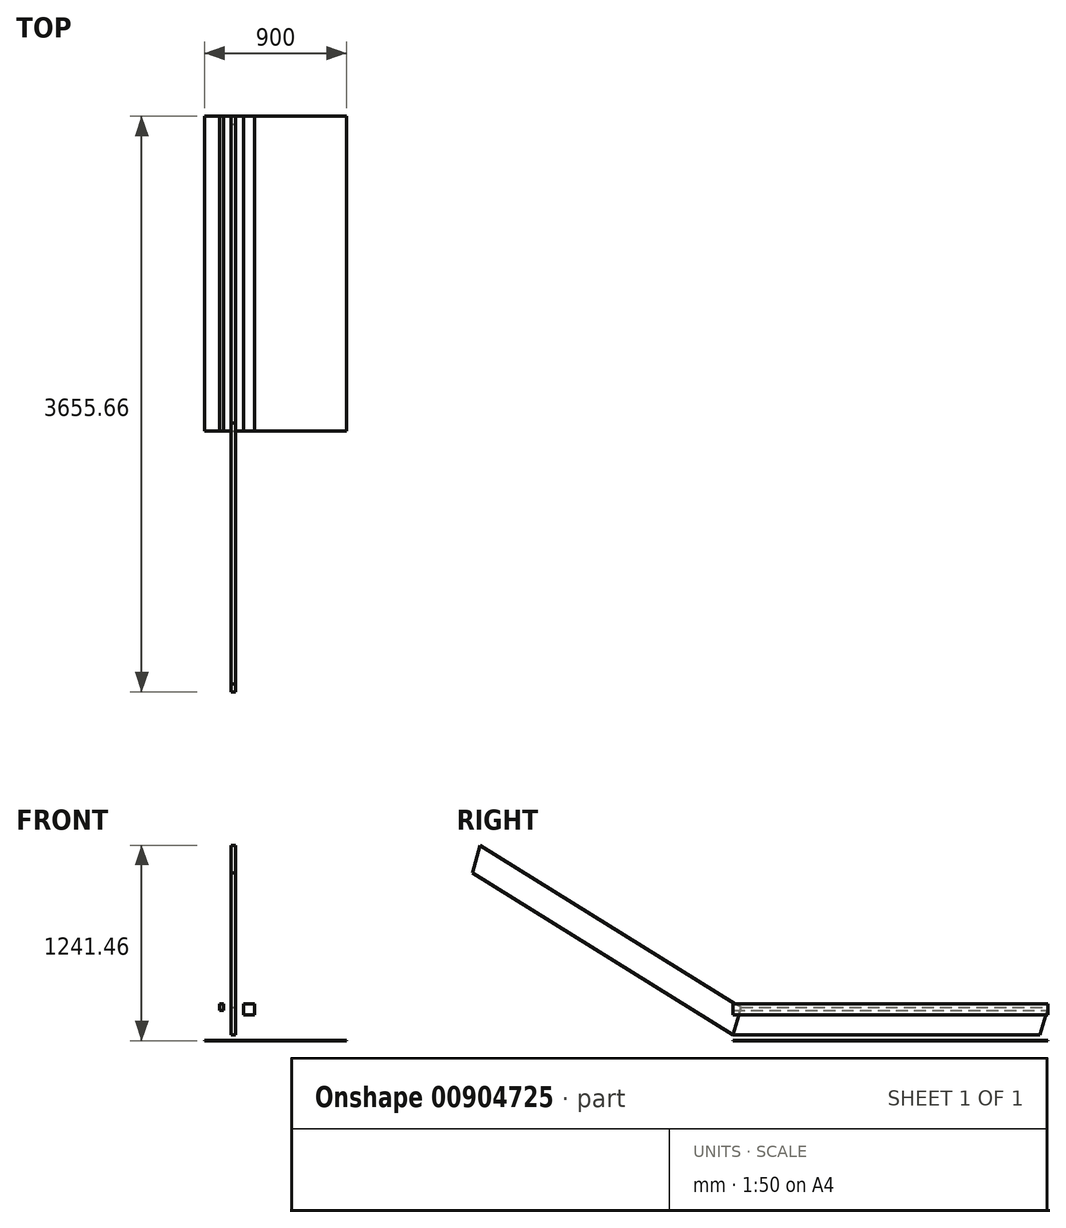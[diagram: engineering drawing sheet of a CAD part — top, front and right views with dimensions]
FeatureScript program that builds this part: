
annotation { "Feature Type Name" : "Feature", "Feature Type Description" : "" }
export const myFeature = defineFeature(function(context is Context, id is Id, definition is map)
    precondition{}
    {
        {
            var Q0;
            Q0=qCreatedBy(makeId("Front.planeOp"),FACE);
            var sketch = newSketch(context, id + "F0", { "sketchPlane" : qUnion([Q0])});
            skLineSegment(sketch, "E0.bottom", {"start": v(0, 0) * mm, "end": v(70, 0) * mm});
            skLineSegment(sketch, "E0.top", {"start": v(0, 70) * mm, "end": v(70, 70) * mm});
            skLineSegment(sketch, "E0.left", {"start": v(0, 0) * mm, "end": v(0, 70) * mm});
            skLineSegment(sketch, "E0.right", {"start": v(70, 0) * mm, "end": v(70, 70) * mm});
            skSolve(sketch);
        }
        {
            var Q0;
            Q0 = qSketchRegion(id + "F0", true);
            extrude(context, id + "F1", {"entities" : qUnion([Q0]), "depth" : 2000 * mm, "offsetDistance" : 25 * mm});
        }
        {
            var Q0;
            Q0=qCreatedBy(makeId("Front.planeOp"),FACE);
            var sketch = newSketch(context, id + "F2", { "sketchPlane" : qUnion([Q0])});
            skLineSegment(sketch, "E1.bottom", {"start": v(-81.08, 45.95) * mm, "end": v(-51.08, 45.95) * mm});
            skLineSegment(sketch, "E1.top", {"start": v(-81.08, -129.05) * mm, "end": v(-51.08, -129.05) * mm});
            skLineSegment(sketch, "E1.left", {"start": v(-81.08, 45.95) * mm, "end": v(-81.08, -129.05) * mm});
            skLineSegment(sketch, "E1.right", {"start": v(-51.08, 45.95) * mm, "end": v(-51.08, -129.05) * mm});
            skSolve(sketch);
        }
        {
            var Q0;
            Q0 = qSketchRegion(id + "F2", true);
            extrude(context, id + "F3", {"entities" : qUnion([Q0]), "depth" : 2000 * mm, "offsetDistance" : 25 * mm});
        }
        {
            var Q0;
            Q0=qCreatedBy(makeId("Front.planeOp"),FACE);
            var sketch = newSketch(context, id + "F4", { "sketchPlane" : qUnion([Q0])});
            skLineSegment(sketch, "E2.bottom", {"start": v(-153.6, 67.64) * mm, "end": v(-126.6, 67.64) * mm});
            skLineSegment(sketch, "E2.top", {"start": v(-153.6, 27.64) * mm, "end": v(-126.6, 27.64) * mm});
            skLineSegment(sketch, "E2.left", {"start": v(-153.6, 67.64) * mm, "end": v(-153.6, 27.64) * mm});
            skLineSegment(sketch, "E2.right", {"start": v(-126.6, 67.64) * mm, "end": v(-126.6, 27.64) * mm});
            skSolve(sketch);
        }
        {
            var Q0;
            Q0 = qSketchRegion(id + "F4", true);
            extrude(context, id + "F5", {"entities" : qUnion([Q0]), "depth" : 2000 * mm, "offsetDistance" : 25 * mm});
        }
        {
            var Q0;
            Q0=qCreatedBy(makeId("Front.planeOp"),FACE);
            var sketch = newSketch(context, id + "F6", { "sketchPlane" : qUnion([Q0])});
            skLineSegment(sketch, "E3.bottom", {"start": v(-247.4, -162.32) * mm, "end": v(652.6, -162.32) * mm});
            skLineSegment(sketch, "E3.top", {"start": v(-247.4, -165.32) * mm, "end": v(652.6, -165.32) * mm});
            skLineSegment(sketch, "E3.left", {"start": v(-247.4, -162.32) * mm, "end": v(-247.4, -165.32) * mm});
            skLineSegment(sketch, "E3.right", {"start": v(652.6, -162.32) * mm, "end": v(652.6, -165.32) * mm});
            skSolve(sketch);
        }
        {
            var Q0;
            Q0 = qSketchRegion(id + "F6", true);
            extrude(context, id + "F7", {"entities" : qUnion([Q0]), "depth" : 2000 * mm, "offsetDistance" : 25 * mm});
        }
        {
            var Q0;
            Q0=makeQuery(id+"F3.opExtrude","SWEPT_FACE",FACE,{"disambiguationData":[OSD([sQuery(id+"F2.wireOp",EDGE,"E1.right")])]});
            var sketch = newSketch(context, id + "F8", { "sketchPlane" : qUnion([Q0])});
            skLineSegment(sketch, "E4", {"start": v(-2000, -129.05) * mm, "end": v(-2000, 45.95) * mm});
            skLineSegment(sketch, "E5", {"start": v(-2000, 45.95) * mm, "end": v(-1950, 45.95) * mm});
            skLineSegment(sketch, "E6", {"start": v(-1950, 45.95) * mm, "end": v(-2000, -129.05) * mm});
            skLineSegment(sketch, "E7", {"start": v(0, 45.95) * mm, "end": v(0, -129.05) * mm});
            skLineSegment(sketch, "E8", {"start": v(0, -129.05) * mm, "end": v(-50, -129.05) * mm});
            skLineSegment(sketch, "E9", {"start": v(-50, -129.05) * mm, "end": v(0, 45.95) * mm});
            skSolve(sketch);
        }
        {
            var Q0;
            Q0=makeQuery(id+"F8.imprint","IMPRINT",FACE,{"disambiguationData":[TD([[makeQuery(id+"F8.imprint","IMPRINT",EDGE,{"derivedFrom":sQuery(id+"F8.wireOp",EDGE,"E7")}),-1.0]])]});
            var Q1;
            Q1=makeQuery(id+"F8.imprint","IMPRINT",FACE,{"disambiguationData":[TD([[makeQuery(id+"F8.imprint","IMPRINT",EDGE,{"derivedFrom":sQuery(id+"F8.wireOp",EDGE,"E4")}),1.0]])]});
            extrude(context, id + "F9", {"entities" : qUnion([Q0, Q1]), "operationType" : NewBodyOperationType.REMOVE, "endBound" : BoundingType.UP_TO_NEXT, "oppositeDirection" : true, "depth" : 25 * mm, "offsetDistance" : 25 * mm});
        }
        {
            var Q0;
            Q0=makeQuery(id+"F3.opExtrude","SWEPT_BODY",BODY,{"disambiguationData":[OSD([sQuery(id+"F2.wireOp",EDGE,"E1.bottom"),sQuery(id+"F2.wireOp",EDGE,"E1.top"),sQuery(id+"F2.wireOp",EDGE,"E1.left"),sQuery(id+"F2.wireOp",EDGE,"E1.right")])]});
            var Q1;
            Q1=makeQuery(id+"F9.boolean.opBoolean","COPY",FACE,{"derivedFrom":makeQuery(id+"F9.opExtrude","SWEPT_FACE",FACE,{"disambiguationData":[OSD([sQuery(id+"F8.wireOp",EDGE,"E6")])]})});
            mirror(context, id + "F10", {"operationType" : NewBodyOperationType.ADD, "entities" : qUnion([Q0]), "mirrorPlane" : qUnion([Q1])});
        }
    });
